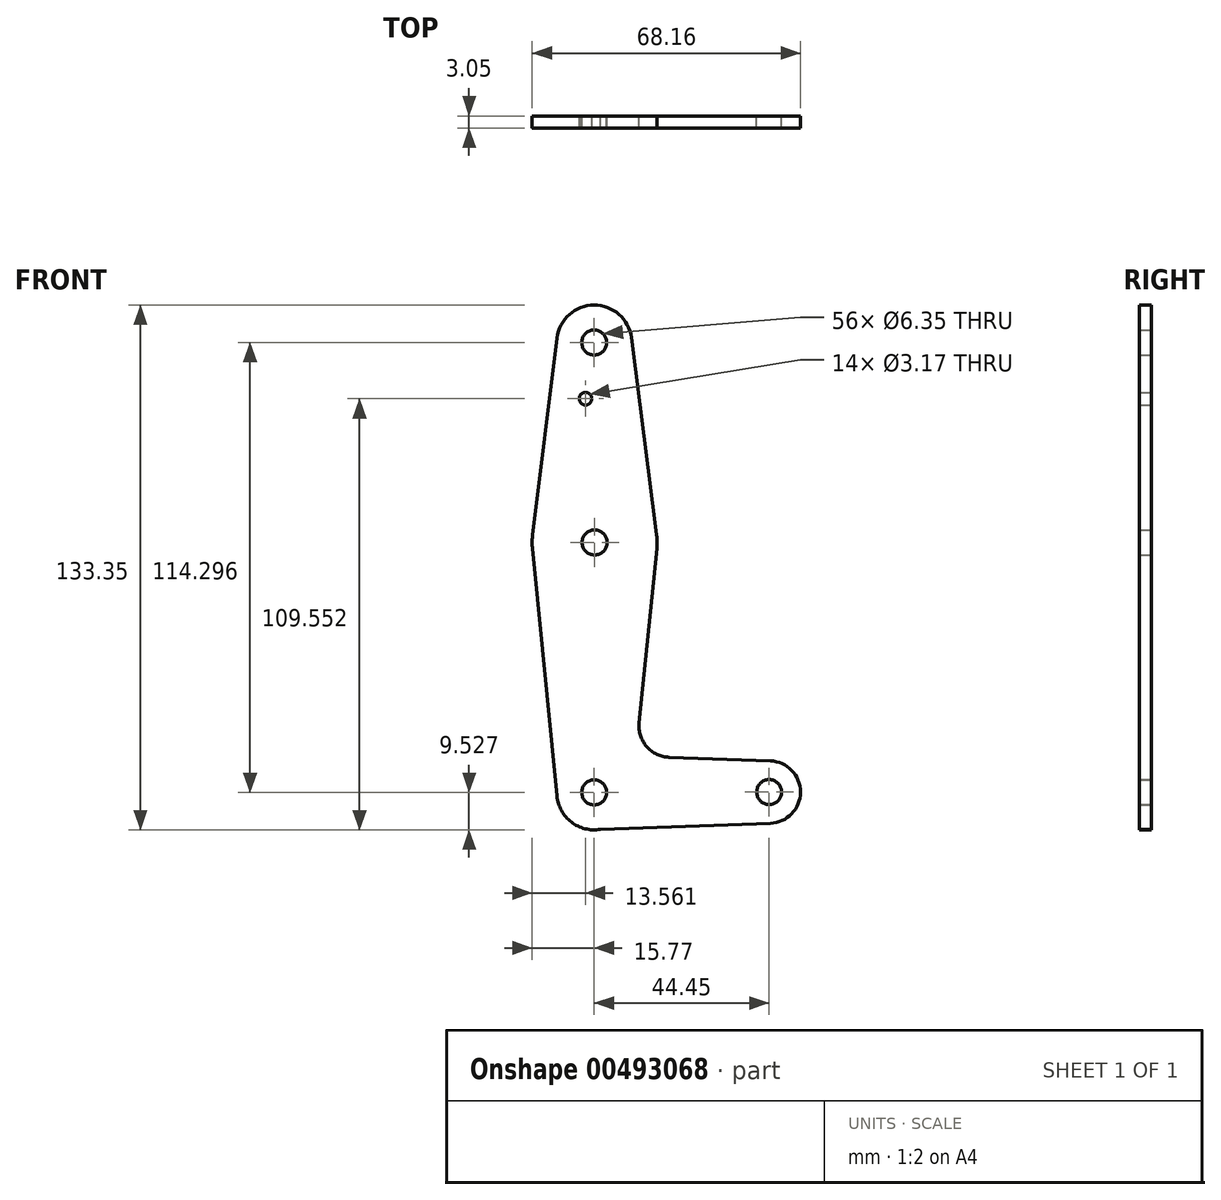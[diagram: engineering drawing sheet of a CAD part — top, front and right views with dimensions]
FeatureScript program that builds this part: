
annotation { "Feature Type Name" : "Feature", "Feature Type Description" : "" }
export const myFeature = defineFeature(function(context is Context, id is Id, definition is map)
    precondition{}
    {
        {
            var Q0;
            Q0=qCreatedBy(makeId("Front.planeOp"),FACE);
            var sketch = newSketch(context, id + "F0", { "sketchPlane" : qUnion([Q0])});
            skCircle(sketch, "E0", {"center": v(0, 47.62) * mm, "radius": 9.53 * mm});
            skCircle(sketch, "E1", {"center": v(0.1, -3.17) * mm, "radius": 15.88 * mm});
            skCircle(sketch, "E2", {"center": v(0, -66.67) * mm, "radius": 9.53 * mm});
            skCircle(sketch, "E3", {"center": v(44.45, -66.6) * mm, "radius": 7.94 * mm});
            skLineSegment(sketch, "E4", {"start": v(-9.45, 48.8) * mm, "end": v(-15.65, -1.22) * mm});
            skLineSegment(sketch, "E5", {"start": v(11.42, -49.01) * mm, "end": v(15.9, -4.77) * mm});
            skLineSegment(sketch, "E6", {"start": v(19.05, -57.76) * mm, "end": v(44.73, -58.67) * mm});
            skLineSegment(sketch, "E7", {"start": v(1.54, -76.07) * mm, "end": v(44.73, -74.54) * mm});
            skCircle(sketch, "E8", {"center": v(0, 47.62) * mm, "radius": 3.18 * mm});
            skCircle(sketch, "E9", {"center": v(0.1, -3.17) * mm, "radius": 3.18 * mm});
            skCircle(sketch, "E10", {"center": v(0, -66.67) * mm, "radius": 3.18 * mm});
            skCircle(sketch, "E11", {"center": v(44.45, -66.6) * mm, "radius": 3.18 * mm});
            skCircle(sketch, "E12", {"center": v(-2.2, 33.35) * mm, "radius": 1.59 * mm});
            skArc(sketch, "E13.filletArc", {"start": v(11.42, -49.01) * mm, "mid": v(13.34, -55.04) * mm, "end": v(19.05, -57.76) * mm});
            skLineSegment(sketch, "E14", {"start": v(-15.7, -4.73) * mm, "end": v(-9.48, -67.6) * mm});
            skLineSegment(sketch, "E15", {"start": v(9.45, 48.83) * mm, "end": v(15.85, -1.16) * mm});
            skSolve(sketch);
        }
        {
            var Q0;
            Q0 = qSketchRegion(id + "F0", true);
            extrude(context, id + "F1", {"entities" : qUnion([Q0]), "depth" : 3.05 * mm});
        }
    });
